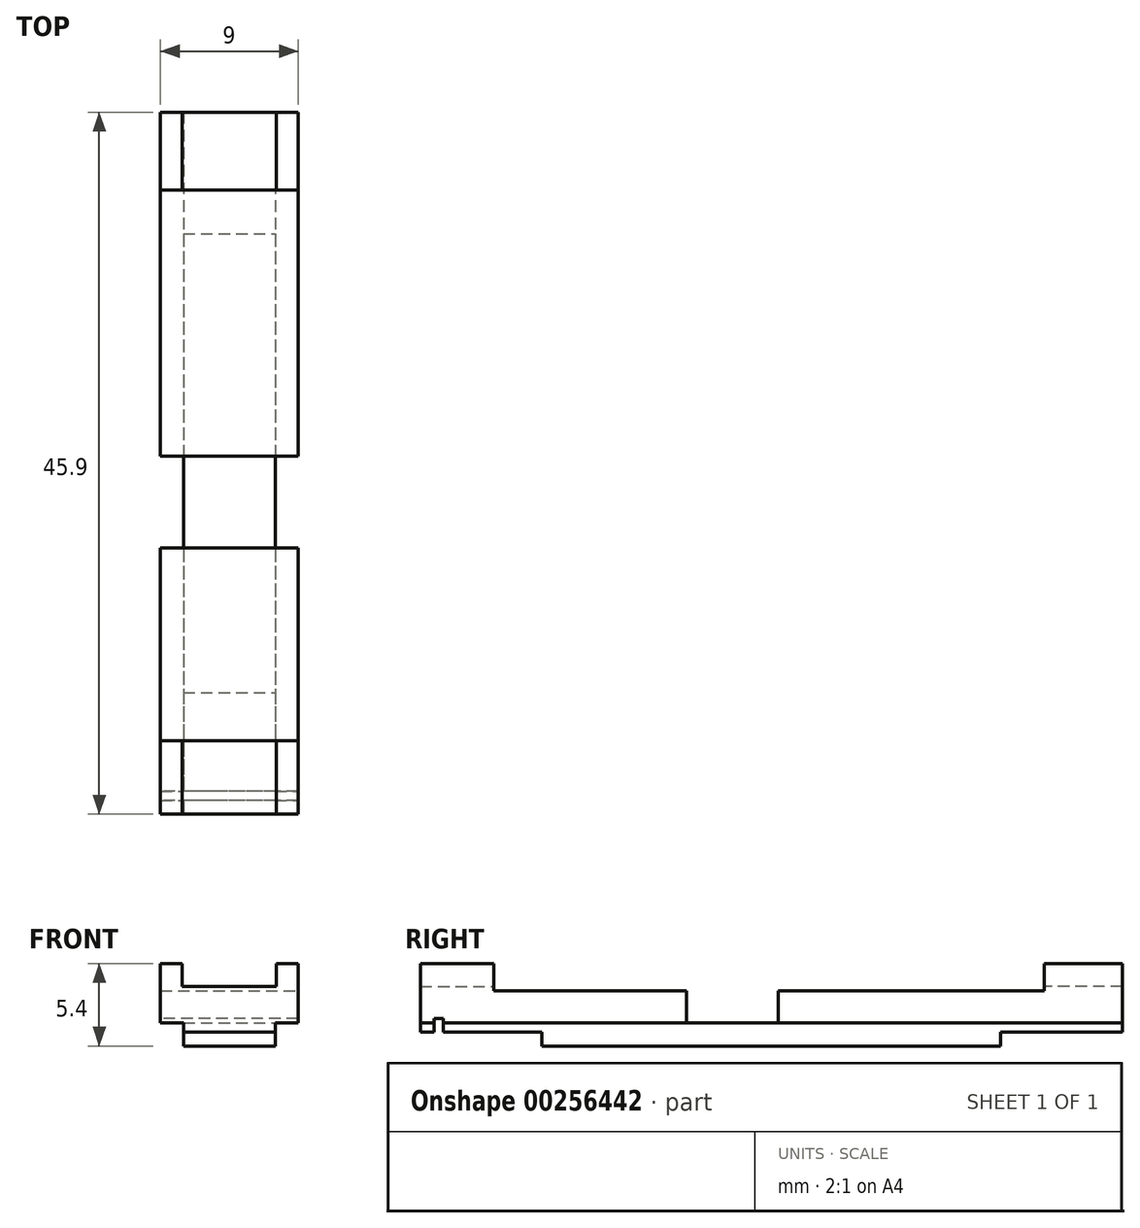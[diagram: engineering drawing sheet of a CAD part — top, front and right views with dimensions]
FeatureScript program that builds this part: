
annotation { "Feature Type Name" : "Feature", "Feature Type Description" : "" }
export const myFeature = defineFeature(function(context is Context, id is Id, definition is map)
    precondition{}
    {
        {
            var Q0;
            Q0=qCreatedBy(makeId("Top.planeOp"),FACE);
            var sketch = newSketch(context, id + "F0", { "sketchPlane" : qUnion([Q0])});
            skLineSegment(sketch, "E0.bottom", {"start": v(-1, 5) * mm, "end": v(1, 5) * mm});
            skLineSegment(sketch, "E0.top", {"start": v(-1, -5) * mm, "end": v(1, -5) * mm});
            skLineSegment(sketch, "E0.left", {"start": v(-1, 5) * mm, "end": v(-1, -5) * mm});
            skLineSegment(sketch, "E0.right", {"start": v(1, 5) * mm, "end": v(1, -5) * mm});
            skSolve(sketch);
        }
        {
            var Q0;
            Q0=makeQuery(id+"F0.imprint","IMPRINT",FACE,{"disambiguationData":[TD([[makeQuery(id+"F0.imprint","IMPRINT",EDGE,{"derivedFrom":sQuery(id+"F0.wireOp",EDGE,"E0.bottom")}),-1.0]])]});
            extrude(context, id + "F1", {"entities" : qUnion([Q0]), "depth" : 0.3 * mm});
        }
        {
            var Q0;
            Q0=makeQuery(id+"F1.opExtrude","CAP_FACE",FACE,{"disambiguationData":[OSD([sQuery(id+"F0.wireOp",EDGE,"E0.bottom"),sQuery(id+"F0.wireOp",EDGE,"E0.top"),sQuery(id+"F0.wireOp",EDGE,"E0.left"),sQuery(id+"F0.wireOp",EDGE,"E0.right")])],"isStart":false});
            var sketch = newSketch(context, id + "F2", { "sketchPlane" : qUnion([Q0])});
            skLineSegment(sketch, "E1.bottom", {"start": v(-1, 7.65) * mm, "end": v(1, 7.65) * mm});
            skLineSegment(sketch, "E1.top", {"start": v(-1, -7.65) * mm, "end": v(1, -7.65) * mm});
            skLineSegment(sketch, "E1.left", {"start": v(-1, 7.65) * mm, "end": v(-1, -7.65) * mm});
            skLineSegment(sketch, "E1.right", {"start": v(1, 7.65) * mm, "end": v(1, -7.65) * mm});
            skSolve(sketch);
        }
        {
            var Q0;
            {var subQ2=sQuery(id+"F2.wireOp",EDGE,"E1.bottom");Q0=makeQuery(id+"F2.imprint","IMPRINT",FACE,{"disambiguationData":[TD([[makeQuery(id+"F2.imprint","IMPRINT",EDGE,{"derivedFrom":subQ2}),-1.0]])]});}
            var Q1;
            {var subQ1=makeQuery(id+"F1.opExtrude","CAP_EDGE",EDGE,{"disambiguationData":[OSD([sQuery(id+"F0.wireOp",EDGE,"E0.bottom")])],"isStart":false});Q1=makeQuery(id+"F2.imprint","IMPRINT",FACE,{"disambiguationData":[TD([[makeQuery(id+"F2.imprint","IMPRINT",EDGE,{"derivedFrom":subQ1}),-1.0]])]});}
            var Q2;
            {var subQ2=sQuery(id+"F2.wireOp",EDGE,"E1.top");Q2=makeQuery(id+"F2.imprint","IMPRINT",FACE,{"disambiguationData":[TD([[makeQuery(id+"F2.imprint","IMPRINT",EDGE,{"derivedFrom":subQ2}),1.0]])]});}
            extrude(context, id + "F3", {"entities" : qUnion([Q0, Q1, Q2]), "operationType" : NewBodyOperationType.ADD, "depth" : 0.2 * mm});
        }
        {
            var Q0;
            Q0=makeQuery(id+"F3.opExtrude","CAP_FACE",FACE,{"disambiguationData":[OSD([sQuery(id+"F2.wireOp",EDGE,"E1.bottom"),sQuery(id+"F2.wireOp",EDGE,"E1.top"),sQuery(id+"F2.wireOp",EDGE,"E1.left"),sQuery(id+"F2.wireOp",EDGE,"E1.right")])],"isStart":false});
            var sketch = newSketch(context, id + "F4", { "sketchPlane" : qUnion([Q0])});
            skLineSegment(sketch, "E2.bottom", {"start": v(-1.5, 7.65) * mm, "end": v(1.5, 7.65) * mm});
            skLineSegment(sketch, "E2.top", {"start": v(-1.5, 0.15) * mm, "end": v(1.5, 0.15) * mm});
            skLineSegment(sketch, "E2.left", {"start": v(-1.5, 7.65) * mm, "end": v(-1.5, 0.15) * mm});
            skLineSegment(sketch, "E2.right", {"start": v(1.5, 7.65) * mm, "end": v(1.5, 0.15) * mm});
            skLineSegment(sketch, "E3.bottom", {"start": v(-1.5, -7.65) * mm, "end": v(1.5, -7.65) * mm});
            skLineSegment(sketch, "E3.top", {"start": v(-1.5, -1.85) * mm, "end": v(1.5, -1.85) * mm});
            skLineSegment(sketch, "E3.left", {"start": v(-1.5, -7.65) * mm, "end": v(-1.5, -1.85) * mm});
            skLineSegment(sketch, "E3.right", {"start": v(1.5, -7.65) * mm, "end": v(1.5, -1.85) * mm});
            skSolve(sketch);
        }
        {
            var Q0;
            {var subQ0=makeQuery(id+"F3.opExtrude","CAP_EDGE",EDGE,{"disambiguationData":[OSD([sQuery(id+"F2.wireOp",EDGE,"E1.left")])],"isStart":false});var subQ3=sQuery(id+"F4.wireOp",EDGE,"E2.bottom");var subQ4=makeQuery(id+"F4.imprint","INTERSECT",VERTEX,{"derivedFrom":[subQ0,subQ3]});var subQ6=sQuery(id+"F4.wireOp",EDGE,"E2.left");var subQ7=sQuery(id+"F4.wireOp",EDGE,"E2.right");var subQ14=sQuery(id+"F4.wireOp",EDGE,"E3.bottom");var subQ15=makeQuery(id+"F4.imprint","INTERSECT",VERTEX,{"derivedFrom":[subQ0,subQ14]});var subQ17=sQuery(id+"F4.wireOp",EDGE,"E3.left");var subQ18=sQuery(id+"F4.wireOp",EDGE,"E3.right");Q0=qUnion([makeQuery(id+"F4.imprint","IMPRINT",FACE,{"disambiguationData":[TD([[makeQuery(id+"F4.imprint","IMPRINT",EDGE,{"derivedFrom":subQ6}),1.0]])]}),makeQuery(id+"F4.imprint","IMPRINT",FACE,{"disambiguationData":[TD([[makeQuery(id+"F4.imprint","IMPRINT",EDGE,{"derivedFrom":subQ7}),-1.0]])]}),makeQuery(id+"F4.imprint","IMPRINT",FACE,{"disambiguationData":[TD([[makeQuery(id+"F4.imprint","IMPRINT",EDGE,{"derivedFrom":subQ17}),-1.0]])]}),makeQuery(id+"F4.imprint","IMPRINT",FACE,{"disambiguationData":[TD([[makeQuery(id+"F4.imprint","IMPRINT",EDGE,{"derivedFrom":subQ18}),1.0]])]}),makeQuery(id+"F4.imprint","IMPRINT",FACE,{"disambiguationData":[TD([[makeQuery(id+"F4.imprint","IMPRINT",EDGE,{"disambiguationData":[TD([[subQ4,-1.0]])],"derivedFrom":subQ3}),-1.0]])]}),makeQuery(id+"F4.imprint","IMPRINT",FACE,{"disambiguationData":[TD([[makeQuery(id+"F4.imprint","IMPRINT",EDGE,{"disambiguationData":[TD([[subQ15,-1.0]])],"derivedFrom":subQ14}),1.0]])]})]);}
            extrude(context, id + "F5", {"entities" : qUnion([Q0]), "operationType" : NewBodyOperationType.ADD, "depth" : 0.7 * mm});
        }
        {
            var Q0;
            Q0=makeQuery(id+"F5.opExtrude","CAP_FACE",FACE,{"disambiguationData":[OSD([sQuery(id+"F4.wireOp",EDGE,"E3.bottom"),sQuery(id+"F4.wireOp",EDGE,"E3.top"),sQuery(id+"F4.wireOp",EDGE,"E3.left"),sQuery(id+"F4.wireOp",EDGE,"E3.right")])],"isStart":false});
            var sketch = newSketch(context, id + "F6", { "sketchPlane" : qUnion([Q0])});
            skLineSegment(sketch, "E4.bottom", {"start": v(-1.5, 7.65) * mm, "end": v(1.5, 7.65) * mm});
            skLineSegment(sketch, "E4.top", {"start": v(-1.5, 5.95) * mm, "end": v(1.5, 5.95) * mm});
            skLineSegment(sketch, "E4.left", {"start": v(-1.5, 7.65) * mm, "end": v(-1.5, 5.95) * mm});
            skLineSegment(sketch, "E4.right", {"start": v(1.5, 7.65) * mm, "end": v(1.5, 5.95) * mm});
            skLineSegment(sketch, "E5.bottom", {"start": v(-1.5, -7.65) * mm, "end": v(1.5, -7.65) * mm});
            skLineSegment(sketch, "E5.top", {"start": v(-1.5, -6.05) * mm, "end": v(1.5, -6.05) * mm});
            skLineSegment(sketch, "E5.left", {"start": v(-1.5, -7.65) * mm, "end": v(-1.5, -6.05) * mm});
            skLineSegment(sketch, "E5.right", {"start": v(1.5, -7.65) * mm, "end": v(1.5, -6.05) * mm});
            skSolve(sketch);
        }
        {
            var Q0;
            {Q0=qUnion([makeQuery(id+"F6.imprint","IMPRINT",FACE,{"disambiguationData":[TD([[makeQuery(id+"F6.imprint","IMPRINT",EDGE,{"derivedFrom":sQuery(id+"F6.wireOp",EDGE,"E4.bottom")}),-1.0]])]}),makeQuery(id+"F6.imprint","IMPRINT",FACE,{"disambiguationData":[TD([[makeQuery(id+"F6.imprint","IMPRINT",EDGE,{"derivedFrom":sQuery(id+"F6.wireOp",EDGE,"E5.bottom")}),1.0]])]})]);}
            extrude(context, id + "F7", {"entities" : qUnion([Q0]), "operationType" : NewBodyOperationType.ADD, "depth" : 0.1 * mm});
        }
        {
            var Q0;
            Q0=makeQuery(id+"F7.opExtrude","CAP_FACE",FACE,{"disambiguationData":[OSD([sQuery(id+"F6.wireOp",EDGE,"E5.bottom"),sQuery(id+"F6.wireOp",EDGE,"E5.top"),sQuery(id+"F6.wireOp",EDGE,"E5.left"),sQuery(id+"F6.wireOp",EDGE,"E5.right")])],"isStart":false});
            var sketch = newSketch(context, id + "F8", { "sketchPlane" : qUnion([Q0])});
            skLineSegment(sketch, "E6.bottom", {"start": v(-1.5, 7.65) * mm, "end": v(-1.02, 7.65) * mm});
            skLineSegment(sketch, "E6.top", {"start": v(-1.5, 5.95) * mm, "end": v(-1.03, 5.95) * mm});
            skLineSegment(sketch, "E6.left", {"start": v(-1.5, 7.65) * mm, "end": v(-1.5, 5.95) * mm});
            skLineSegment(sketch, "E6.right", {"start": v(-1.02, 7.65) * mm, "end": v(-1.03, 5.95) * mm});
            skLineSegment(sketch, "E7.bottom", {"start": v(1.5, 7.65) * mm, "end": v(1.02, 7.65) * mm});
            skLineSegment(sketch, "E7.top", {"start": v(1.5, 5.95) * mm, "end": v(1.03, 5.95) * mm});
            skLineSegment(sketch, "E7.left", {"start": v(1.5, 7.65) * mm, "end": v(1.5, 5.95) * mm});
            skLineSegment(sketch, "E7.right", {"start": v(1.02, 7.65) * mm, "end": v(1.03, 5.95) * mm});
            skLineSegment(sketch, "E8.bottom", {"start": v(-1.5, -7.65) * mm, "end": v(-1.03, -7.65) * mm});
            skLineSegment(sketch, "E8.top", {"start": v(-1.5, -6.05) * mm, "end": v(-1.03, -6.05) * mm});
            skLineSegment(sketch, "E8.left", {"start": v(-1.5, -7.65) * mm, "end": v(-1.5, -6.05) * mm});
            skLineSegment(sketch, "E8.right", {"start": v(-1.03, -7.65) * mm, "end": v(-1.03, -6.05) * mm});
            skLineSegment(sketch, "E9.bottom", {"start": v(1.5, -7.65) * mm, "end": v(1.03, -7.65) * mm});
            skLineSegment(sketch, "E9.top", {"start": v(1.5, -6.05) * mm, "end": v(1.03, -6.05) * mm});
            skLineSegment(sketch, "E9.left", {"start": v(1.5, -7.65) * mm, "end": v(1.5, -6.05) * mm});
            skLineSegment(sketch, "E9.right", {"start": v(1.03, -7.65) * mm, "end": v(1.03, -6.05) * mm});
            skSolve(sketch);
        }
        {
            var Q0;
            {Q0=qUnion([makeQuery(id+"F8.imprint","IMPRINT",FACE,{"disambiguationData":[TD([[makeQuery(id+"F8.imprint","IMPRINT",EDGE,{"derivedFrom":sQuery(id+"F8.wireOp",EDGE,"E6.bottom")}),-1.0]])]}),makeQuery(id+"F8.imprint","IMPRINT",FACE,{"disambiguationData":[TD([[makeQuery(id+"F8.imprint","IMPRINT",EDGE,{"derivedFrom":sQuery(id+"F8.wireOp",EDGE,"E7.bottom")}),1.0]])]}),makeQuery(id+"F8.imprint","IMPRINT",FACE,{"disambiguationData":[TD([[makeQuery(id+"F8.imprint","IMPRINT",EDGE,{"derivedFrom":sQuery(id+"F8.wireOp",EDGE,"E8.bottom")}),1.0]])]}),makeQuery(id+"F8.imprint","IMPRINT",FACE,{"disambiguationData":[TD([[makeQuery(id+"F8.imprint","IMPRINT",EDGE,{"derivedFrom":sQuery(id+"F8.wireOp",EDGE,"E9.bottom")}),1.0]])]})]);}
            extrude(context, id + "F9", {"entities" : qUnion([Q0]), "operationType" : NewBodyOperationType.ADD, "depth" : 0.5 * mm});
        }
        {
            var Q0;
            {var subQ0=sQuery(id+"F2.wireOp",EDGE,"E1.top");var subQ1=sQuery(id+"F2.wireOp",EDGE,"E1.left");var subQ2=sQuery(id+"F2.wireOp",EDGE,"E1.right");Q0=makeQuery(id+"F3.boolean.opBoolean","SPLIT",FACE,{"disambiguationData":[TD([makeQuery(id+"F1.opExtrude","SWEPT_FACE",FACE,{"disambiguationData":[OSD([sQuery(id+"F0.wireOp",EDGE,"E0.top")])]})])],"derivedFrom":makeQuery(id+"F3.opExtrude","CAP_FACE",FACE,{"disambiguationData":[OSD([sQuery(id+"F2.wireOp",EDGE,"E1.bottom"),subQ0,subQ1,subQ2])],"isStart":true})});}
            var sketch = newSketch(context, id + "F10", { "sketchPlane" : qUnion([Q0])});
            skLineSegment(sketch, "E10.bottom", {"start": v(1.5, 7.15) * mm, "end": v(-1.5, 7.15) * mm});
            skLineSegment(sketch, "E10.top", {"start": v(1.5, 7.35) * mm, "end": v(-1.5, 7.35) * mm});
            skLineSegment(sketch, "E10.left", {"start": v(1.5, 7.15) * mm, "end": v(1.5, 7.35) * mm});
            skLineSegment(sketch, "E10.right", {"start": v(-1.5, 7.15) * mm, "end": v(-1.5, 7.35) * mm});
            skSolve(sketch);
        }
        {
            var Q0;
            {var subQ0=sQuery(id+"F2.wireOp",EDGE,"E1.right");var subQ5=makeQuery(id+"F1.opExtrude","SWEPT_FACE",FACE,{"disambiguationData":[OSD([sQuery(id+"F0.wireOp",EDGE,"E0.top")])]});var subQ6=makeQuery(id+"F3.boolean.opBoolean","SPLIT",EDGE,{"disambiguationData":[TD([subQ5])],"derivedFrom":makeQuery(id+"F3.opExtrude","CAP_EDGE",EDGE,{"disambiguationData":[OSD([subQ0])],"isStart":true})});var subQ9=sQuery(id+"F10.wireOp",EDGE,"E10.bottom");var subQ10=makeQuery(id+"F10.imprint","INTERSECT",VERTEX,{"derivedFrom":[subQ6,subQ9]});var subQ12=sQuery(id+"F10.wireOp",EDGE,"E10.left");var subQ17=sQuery(id+"F10.wireOp",EDGE,"E10.right");Q0=qUnion([makeQuery(id+"F10.imprint","IMPRINT",FACE,{"disambiguationData":[TD([[makeQuery(id+"F10.imprint","IMPRINT",EDGE,{"derivedFrom":subQ12}),1.0]])]}),makeQuery(id+"F10.imprint","IMPRINT",FACE,{"disambiguationData":[TD([[makeQuery(id+"F10.imprint","IMPRINT",EDGE,{"derivedFrom":subQ17}),-1.0]])]}),makeQuery(id+"F10.imprint","IMPRINT",FACE,{"disambiguationData":[TD([[makeQuery(id+"F10.imprint","IMPRINT",EDGE,{"disambiguationData":[TD([[subQ10,-1.0]])],"derivedFrom":subQ9}),-1.0]])]})]);}
            extrude(context, id + "F11", {"entities" : qUnion([Q0]), "operationType" : NewBodyOperationType.REMOVE, "oppositeDirection" : true, "depth" : 0.3 * mm});
        }
        {
            var Q0;
            Q0=makeQuery(id+"F1.opExtrude","SWEPT_BODY",BODY,{"disambiguationData":[OSD([sQuery(id+"F0.wireOp",EDGE,"E0.bottom"),sQuery(id+"F0.wireOp",EDGE,"E0.top"),sQuery(id+"F0.wireOp",EDGE,"E0.left"),sQuery(id+"F0.wireOp",EDGE,"E0.right")])]});
            var Q1;
            Q1=qCreatedBy(makeId("Origin.pointOp"),VERTEX);
            transform(context, id + "F12", {"entities" : qUnion([Q0]), "transformType" : TransformType.SCALE_UNIFORMLY, "scale" : 3, "makeCopy" : false, "scalePoint" : qUnion([Q1])});
        }
    });
